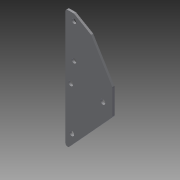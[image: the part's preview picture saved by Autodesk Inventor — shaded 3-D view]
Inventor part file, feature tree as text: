
AUTODESK INVENTOR PART (.ipt)
format: ipt  version: 2013 (Build 170138000, 138)  size: 142,848 bytes
history: native  units: in
note: dims shown in document units (in); Inventor stores cm internally (conversion verified against a paired STEP export)
features: extrude x6, sketch x6, fillet x4
ambient origin geometry x8: Origin, YZ Plane, XZ Plane, XY Plane, X Axis, Y Axis, Z Axis, Center Point
bodies: Solid1 (feature_tree)
feature tree (16):
  extrude  "Extrusion1"  Depth=0.125in TaperAngle=0.0deg
  extrude  "Extrusion2"  Depth=0.28in
  extrude  "Extrusion3"  Depth=0.5in
  fillet  "Fillet2"  Radius=0.56in
  fillet  "Fillet3"  Radius=0.31in
  extrude  "Extrusion4"  Depth=0.266in
  extrude  "Extrusion5"  Depth=0.5in
  fillet  "Fillet4"  Radius=0.5in
  extrude  "Extrusion6"  Depth=2.0in
  fillet  "Fillet5"  Radius=1.0in
  sketch  "Sketch1"  dims[d1=1.5in d3=0.125in d4=0.0in]
  sketch  "Sketch2"  dims[d5=0.28in d6=0.28in]
  sketch  "Sketch3"  dims[d7=0.5in d8=0.5in d9=0.56in d11=0.31in]
  sketch  "Sketch4"  dims[d12=1.0in d13=0.0in d15=0.266in]
  sketch  "Sketch5"  dims[d16=0.266in d17=0.5in d18=0.5in]
  sketch  "Sketch6"  dims[d19=1.737in d20=2.0in d21=1.0in d22=0.0in d23=0.125in d24=3.0in d25=2.75in d26=2.75in d27=0.125in d28=0.266in d29=3.75in d30=0.375in d31=1.0in d32=0.0in d33=1.0in d34=0.0in d36=4.125in d38=0.8344in d39=0.125in d40=30.0deg d41=0.5in d42=1.0in d43=0.0in d44=0.125in]
